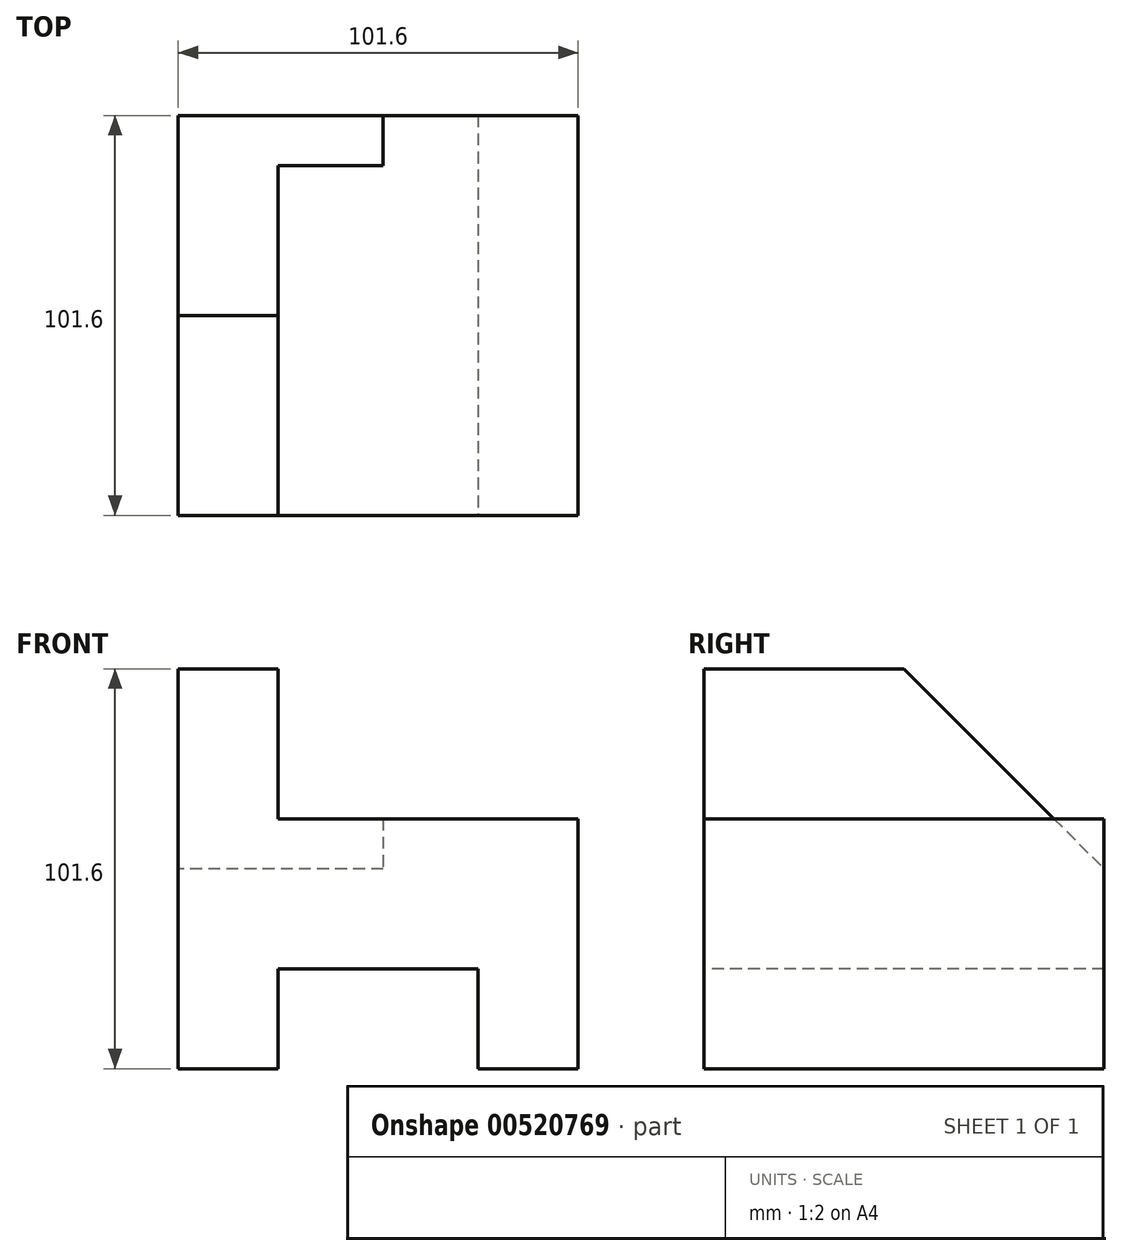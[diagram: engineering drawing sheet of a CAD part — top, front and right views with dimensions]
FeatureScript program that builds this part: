
annotation { "Feature Type Name" : "Feature", "Feature Type Description" : "" }
export const myFeature = defineFeature(function(context is Context, id is Id, definition is map)
    precondition{}
    {
        {
            var Q0;
            Q0=qCreatedBy(makeId("Top.planeOp"),FACE);
            var sketch = newSketch(context, id + "F0", { "sketchPlane" : qUnion([Q0])});
            skLineSegment(sketch, "E0.bottom", {"start": v(-50.8, -50.8) * mm, "end": v(50.8, -50.8) * mm});
            skLineSegment(sketch, "E0.top", {"start": v(-50.8, 50.8) * mm, "end": v(50.8, 50.8) * mm});
            skLineSegment(sketch, "E0.left", {"start": v(-50.8, -50.8) * mm, "end": v(-50.8, 50.8) * mm});
            skLineSegment(sketch, "E0.right", {"start": v(50.8, -50.8) * mm, "end": v(50.8, 50.8) * mm});
            skPoint(sketch, "E0.middle", {"position": v(0, 0) * mm});
            skSolve(sketch);
        }
        {
            var Q0;
            Q0 = qSketchRegion(id + "F0", true);
            extrude(context, id + "F1", {"entities" : qUnion([Q0]), "depth" : 101.6 * mm, "offsetDistance" : 25.4 * mm});
        }
        {
            var Q0;
            Q0=makeQuery(id+"F1.opExtrude","SWEPT_FACE",FACE,{"disambiguationData":[OSD([sQuery(id+"F0.wireOp",EDGE,"E0.bottom")])]});
            var sketch = newSketch(context, id + "F2", { "sketchPlane" : qUnion([Q0])});
            skLineSegment(sketch, "E1.bottom", {"start": v(-50.8, 0) * mm, "end": v(-25.4, 0) * mm});
            skLineSegment(sketch, "E1.top", {"start": v(-50.8, 25.4) * mm, "end": v(-25.4, 25.4) * mm});
            skLineSegment(sketch, "E1.left", {"start": v(-50.8, 0) * mm, "end": v(-50.8, 25.4) * mm});
            skLineSegment(sketch, "E1.right", {"start": v(-25.4, 0) * mm, "end": v(-25.4, 25.4) * mm});
            skLineSegment(sketch, "E2.bottom", {"start": v(-25.4, 25.4) * mm, "end": v(0, 25.4) * mm});
            skLineSegment(sketch, "E2.top", {"start": v(-25.4, 0) * mm, "end": v(0, 0) * mm});
            skLineSegment(sketch, "E2.left", {"start": v(-25.4, 25.4) * mm, "end": v(-25.4, 0) * mm});
            skLineSegment(sketch, "E2.right", {"start": v(0, 25.4) * mm, "end": v(0, 0) * mm});
            skLineSegment(sketch, "E3.bottom", {"start": v(0, 25.4) * mm, "end": v(25.4, 25.4) * mm});
            skLineSegment(sketch, "E3.top", {"start": v(0, 0) * mm, "end": v(25.4, 0) * mm});
            skLineSegment(sketch, "E3.right", {"start": v(25.4, 25.4) * mm, "end": v(25.4, 0) * mm});
            skLineSegment(sketch, "E4", {"start": v(25.4, 25.4) * mm, "end": v(50.8, 25.4) * mm});
            skLineSegment(sketch, "E5", {"start": v(50.8, 25.4) * mm, "end": v(50.8, 0) * mm});
            skLineSegment(sketch, "E6", {"start": v(50.8, 0) * mm, "end": v(25.4, 0) * mm});
            skLineSegment(sketch, "E7.bottom", {"start": v(-25.4, 25.4) * mm, "end": v(-12.7, 25.4) * mm});
            skLineSegment(sketch, "E7.top", {"start": v(-25.4, 0) * mm, "end": v(-12.7, 0) * mm});
            skLineSegment(sketch, "E7.right", {"start": v(-12.7, 25.4) * mm, "end": v(-12.7, 0) * mm});
            skLineSegment(sketch, "E8.bottom", {"start": v(25.4, 25.4) * mm, "end": v(12.7, 25.4) * mm});
            skLineSegment(sketch, "E8.top", {"start": v(25.4, 0) * mm, "end": v(12.7, 0) * mm});
            skLineSegment(sketch, "E8.right", {"start": v(12.7, 25.4) * mm, "end": v(12.7, 0) * mm});
            skSolve(sketch);
        }
        {
            var Q0;
            Q0=makeQuery(id+"F2.imprint","IMPRINT",FACE,{"disambiguationData":[TD([[makeQuery(id+"F2.imprint","IMPRINT",EDGE,{"derivedFrom":sQuery(id+"F2.wireOp",EDGE,"E2.bottom")}),-1.0]])]});
            var Q1;
            Q1=makeQuery(id+"F2.imprint","IMPRINT",FACE,{"disambiguationData":[TD([[makeQuery(id+"F2.imprint","IMPRINT",EDGE,{"derivedFrom":sQuery(id+"F2.wireOp",EDGE,"E3.bottom")}),-1.0]])]});
            extrude(context, id + "F3", {"entities" : qUnion([Q0, Q1]), "operationType" : NewBodyOperationType.REMOVE, "oppositeDirection" : true, "depth" : 101.6 * mm, "offsetDistance" : 25.4 * mm});
        }
        {
            var Q0;
            Q0=makeQuery(id+"F1.opExtrude","SWEPT_FACE",FACE,{"disambiguationData":[OSD([sQuery(id+"F0.wireOp",EDGE,"E0.top")])]});
            var sketch = newSketch(context, id + "F4", { "sketchPlane" : qUnion([Q0])});
            skLineSegment(sketch, "E9.bottom", {"start": v(-50.8, 101.6) * mm, "end": v(25.4, 101.6) * mm});
            skLineSegment(sketch, "E9.top", {"start": v(-50.8, 63.5) * mm, "end": v(25.4, 63.5) * mm});
            skLineSegment(sketch, "E9.left", {"start": v(-50.8, 101.6) * mm, "end": v(-50.8, 63.5) * mm});
            skLineSegment(sketch, "E9.right", {"start": v(25.4, 101.6) * mm, "end": v(25.4, 63.5) * mm});
            skLineSegment(sketch, "E10.bottom", {"start": v(-50.8, 0) * mm, "end": v(-25.4, 0) * mm});
            skLineSegment(sketch, "E10.top", {"start": v(-50.8, 63.5) * mm, "end": v(-25.4, 63.5) * mm});
            skLineSegment(sketch, "E10.left", {"start": v(-50.8, 0) * mm, "end": v(-50.8, 63.5) * mm});
            skLineSegment(sketch, "E10.right", {"start": v(-25.4, 0) * mm, "end": v(-25.4, 63.5) * mm});
            skLineSegment(sketch, "E11.bottom", {"start": v(-25.4, 63.5) * mm, "end": v(25.4, 63.5) * mm});
            skLineSegment(sketch, "E11.top", {"start": v(-25.4, 50.8) * mm, "end": v(25.4, 50.8) * mm});
            skLineSegment(sketch, "E11.left", {"start": v(-25.4, 63.5) * mm, "end": v(-25.4, 50.8) * mm});
            skLineSegment(sketch, "E11.right", {"start": v(25.4, 63.5) * mm, "end": v(25.4, 50.8) * mm});
            skSolve(sketch);
        }
        {
            var Q0;
            Q0=makeQuery(id+"F4.imprint","IMPRINT",FACE,{"disambiguationData":[TD([[makeQuery(id+"F4.imprint","IMPRINT",EDGE,{"derivedFrom":sQuery(id+"F4.wireOp",EDGE,"E9.bottom")}),1.0]])]});
            var Q1;
            Q1=makeQuery(id+"F4.imprint","IMPRINT",FACE,{"disambiguationData":[TD([[makeQuery(id+"F4.imprint","IMPRINT",EDGE,{"derivedFrom":sQuery(id+"F4.wireOp",EDGE,"E11.bottom")}),-1.0]])]});
            extrude(context, id + "F5", {"entities" : qUnion([Q0, Q1]), "operationType" : NewBodyOperationType.REMOVE, "oppositeDirection" : true, "depth" : 425.96 * mm, "offsetDistance" : 25.4 * mm});
        }
        {
            var Q0;
            Q0=makeQuery(id+"F1.opExtrude","SWEPT_FACE",FACE,{"disambiguationData":[OSD([sQuery(id+"F0.wireOp",EDGE,"E0.left")])]});
            var sketch = newSketch(context, id + "F6", { "sketchPlane" : qUnion([Q0])});
            skLineSegment(sketch, "E12.bottom", {"start": v(50.8, 101.6) * mm, "end": v(0, 101.6) * mm});
            skLineSegment(sketch, "E12.top", {"start": v(50.8, 0) * mm, "end": v(0, 0) * mm});
            skLineSegment(sketch, "E12.left", {"start": v(50.8, 101.6) * mm, "end": v(50.8, 0) * mm});
            skLineSegment(sketch, "E12.right", {"start": v(0, 101.6) * mm, "end": v(0, 0) * mm});
            skLineSegment(sketch, "E13.bottom", {"start": v(-50.8, 0) * mm, "end": v(50.8, 0) * mm});
            skLineSegment(sketch, "E13.top", {"start": v(-50.8, 50.8) * mm, "end": v(50.8, 50.8) * mm});
            skLineSegment(sketch, "E13.left", {"start": v(-50.8, 0) * mm, "end": v(-50.8, 50.8) * mm});
            skLineSegment(sketch, "E13.right", {"start": v(50.8, 0) * mm, "end": v(50.8, 50.8) * mm});
            skLineSegment(sketch, "E14", {"start": v(0, 101.6) * mm, "end": v(-50.8, 50.8) * mm});
            skLineSegment(sketch, "E15", {"start": v(-50.8, 101.6) * mm, "end": v(0, 101.6) * mm});
            skSolve(sketch);
        }
        {
            var Q0;
            {var subQ0=sQuery(id+"F6.wireOp",EDGE,"E14");Q0=makeQuery(id+"F6.imprint","IMPRINT",FACE,{"disambiguationData":[TD([[makeQuery(id+"F6.imprint","IMPRINT",EDGE,{"derivedFrom":subQ0}),-1.0]])]});}
            extrude(context, id + "F7", {"entities" : qUnion([Q0]), "operationType" : NewBodyOperationType.REMOVE, "oppositeDirection" : true, "depth" : 52.07 * mm, "offsetDistance" : 25.4 * mm});
        }
    });
